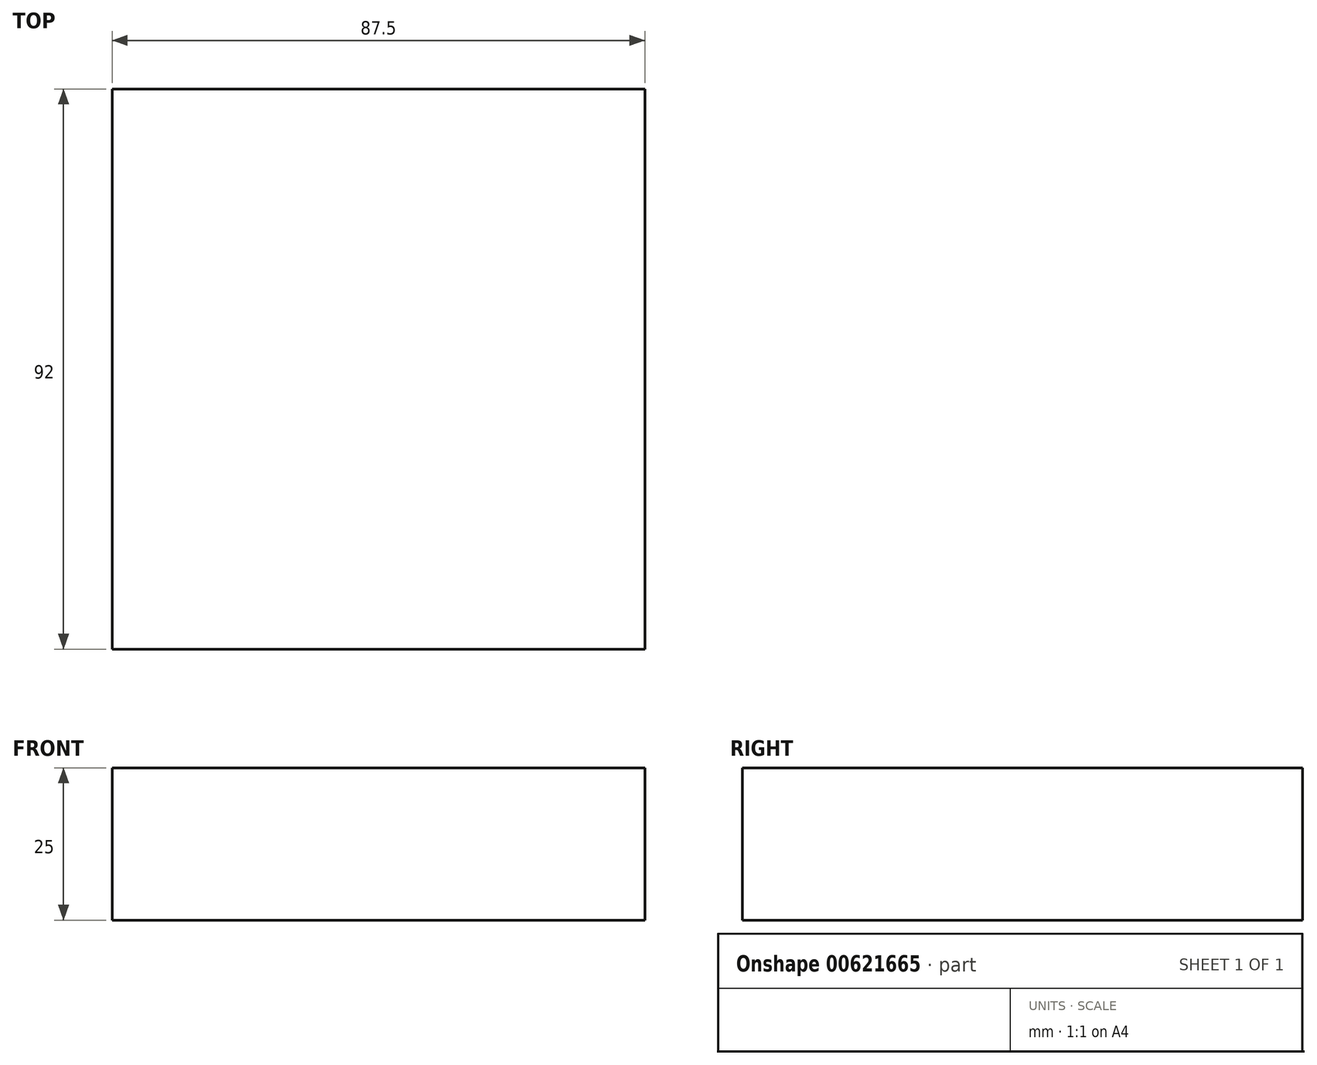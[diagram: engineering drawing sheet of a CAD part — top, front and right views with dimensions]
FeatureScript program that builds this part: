
annotation { "Feature Type Name" : "Feature", "Feature Type Description" : "" }
export const myFeature = defineFeature(function(context is Context, id is Id, definition is map)
    precondition{}
    {
        {
            var Q0;
            Q0=qCreatedBy(makeId("Top.planeOp"),FACE);
            var sketch = newSketch(context, id + "F0", { "sketchPlane" : qUnion([Q0])});
            skLineSegment(sketch, "E0.bottom", {"start": v(-43.75, 46) * mm, "end": v(43.75, 46) * mm});
            skLineSegment(sketch, "E0.top", {"start": v(-43.75, -46) * mm, "end": v(43.75, -46) * mm});
            skLineSegment(sketch, "E0.left", {"start": v(-43.75, 46) * mm, "end": v(-43.75, -46) * mm});
            skLineSegment(sketch, "E0.right", {"start": v(43.75, 46) * mm, "end": v(43.75, -46) * mm});
            skPoint(sketch, "E0.middle", {"position": v(0, 0) * mm});
            skSolve(sketch);
        }
        {
            var Q0;
            Q0 = qSketchRegion(id + "F0", true);
            extrude(context, id + "F1", {"entities" : qUnion([Q0]), "depth" : 25 * mm, "offsetDistance" : 25 * mm});
        }
    });
